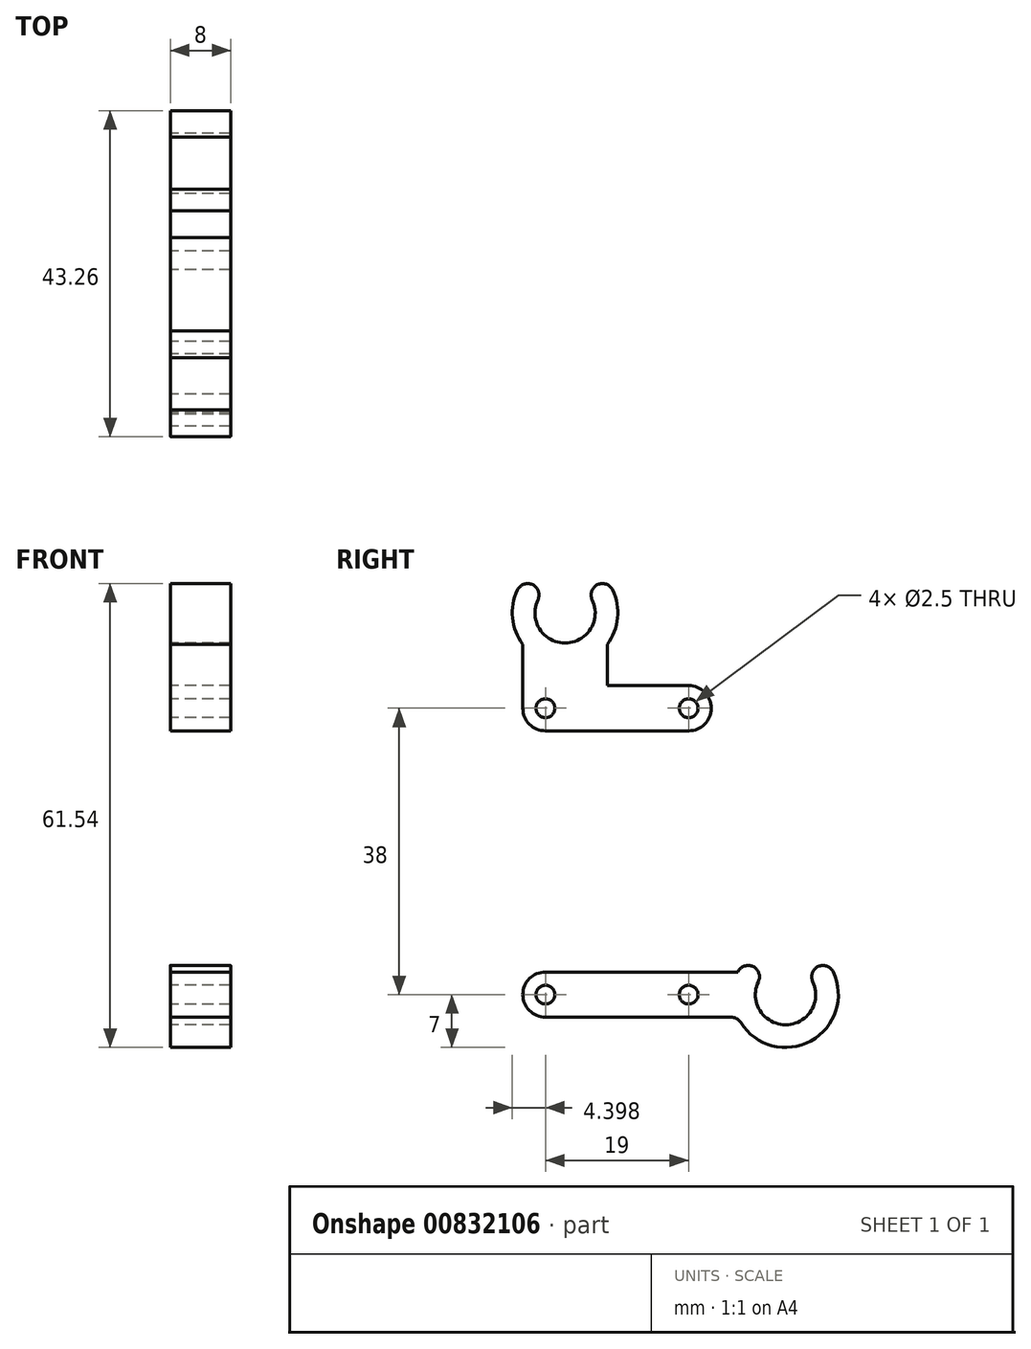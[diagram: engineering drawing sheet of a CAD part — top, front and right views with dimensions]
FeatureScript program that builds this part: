
annotation { "Feature Type Name" : "Feature", "Feature Type Description" : "" }
export const myFeature = defineFeature(function(context is Context, id is Id, definition is map)
    precondition{}
    {
        {
            var Q0;
            Q0=qCreatedBy(makeId("Right.planeOp"),FACE);
            var sketch = newSketch(context, id + "F0", { "sketchPlane" : qUnion([Q0])});
            skArc(sketch, "E0", {"start": v(-3, 53.3) * mm, "mid": v(0, 46.66) * mm, "end": v(3, 53.3) * mm});
            skArc(sketch, "E1", {"start": v(26.26, 2.65) * mm, "mid": v(29.26, -4) * mm, "end": v(32.26, 2.65) * mm});
            skCircle(sketch, "E2", {"center": v(-2.6, 0) * mm, "radius": 1.25 * mm});
            skCircle(sketch, "E3.0.1.0", {"center": v(-2.6, 38) * mm, "radius": 1.25 * mm});
            skCircle(sketch, "E3.1.0.0", {"center": v(16.4, 0) * mm, "radius": 1.25 * mm});
            skCircle(sketch, "E3.1.1.0", {"center": v(16.4, 38) * mm, "radius": 1.25 * mm});
            skLineSegment(sketch, "E3.direction1", {"start": v(-2.6, 0) * mm, "end": v(16.4, 0) * mm, "construction": true});
            skLineSegment(sketch, "E3.direction2", {"start": v(-2.6, 0) * mm, "end": v(-2.6, 38) * mm, "construction": true});
            skLineSegment(sketch, "E4.bottom", {"start": v(-7.8, 43) * mm, "end": v(21.6, 43) * mm, "construction": true});
            skLineSegment(sketch, "E4.top", {"start": v(-7.8, -5) * mm, "end": v(21.6, -5) * mm, "construction": true});
            skLineSegment(sketch, "E4.left", {"start": v(-7.8, 43) * mm, "end": v(-7.8, -5) * mm, "construction": true});
            skLineSegment(sketch, "E4.right", {"start": v(21.6, 43) * mm, "end": v(21.6, -5) * mm, "construction": true});
            skPoint(sketch, "E4.middle", {"position": v(6.9, 19) * mm});
            skPoint(sketch, "E4.middle.positionSnap0", {"position": v(-2.6, 19) * mm});
            skPoint(sketch, "E4.middle.positionSnap1", {"position": v(6.9, 0) * mm});
            skPoint(sketch, "E4.centerSnap0", {"position": v(-2.6, 19) * mm});
            skPoint(sketch, "E4.centerSnap1", {"position": v(6.9, 0) * mm});
            skLineSegment(sketch, "E5", {"start": v(0, 50.66) * mm, "end": v(0, 43) * mm, "construction": true});
            skLineSegment(sketch, "E6", {"start": v(29.26, 0) * mm, "end": v(21.6, 0) * mm, "construction": true});
            skArc(sketch, "E7", {"start": v(-2.6, 3) * mm, "mid": v(-5.6, 0) * mm, "end": v(-2.6, -3) * mm});
            skArc(sketch, "E8", {"start": v(22.94, -3) * mm, "mid": v(33.11, -5.84) * mm, "end": v(34.51, 4.63) * mm});
            skPoint(sketch, "E8.startSnap0", {"position": v(29.26, -4) * mm});
            skLineSegment(sketch, "E9", {"start": v(22.94, -3) * mm, "end": v(-2.6, -3) * mm});
            skLineSegment(sketch, "E10", {"start": v(-2.6, 3) * mm, "end": v(22.94, 3) * mm});
            skLineSegment(sketch, "E11", {"start": v(24.01, 4.63) * mm, "end": v(26.26, 2.65) * mm});
            skLineSegment(sketch, "E12", {"start": v(29.26, 0) * mm, "end": v(32.26, 2.65) * mm, "construction": true});
            skLineSegment(sketch, "E13", {"start": v(29.26, 0) * mm, "end": v(26.26, 2.65) * mm, "construction": true});
            skLineSegment(sketch, "E14", {"start": v(32.26, 2.65) * mm, "end": v(34.51, 4.63) * mm});
            skArc(sketch, "E15", {"start": v(-2.6, 35) * mm, "mid": v(-4.72, 35.88) * mm, "end": v(-5.6, 38) * mm});
            skArc(sketch, "E16", {"start": v(16.4, 41) * mm, "mid": v(19.4, 38) * mm, "end": v(16.4, 35) * mm});
            skLineSegment(sketch, "E17", {"start": v(16.4, 35) * mm, "end": v(-2.6, 35) * mm});
            skArc(sketch, "E18", {"start": v(-5.25, 55.3) * mm, "mid": v(-7, 50.94) * mm, "end": v(-5.6, 46.47) * mm});
            skArc(sketch, "E19", {"start": v(5.25, 55.3) * mm, "mid": v(7, 50.94) * mm, "end": v(5.6, 46.47) * mm});
            skLineSegment(sketch, "E20", {"start": v(-3, 53.3) * mm, "end": v(-5.25, 55.3) * mm});
            skLineSegment(sketch, "E21", {"start": v(3, 53.3) * mm, "end": v(5.25, 55.3) * mm});
            skLineSegment(sketch, "E22", {"start": v(0, 50.66) * mm, "end": v(3, 53.3) * mm, "construction": true});
            skLineSegment(sketch, "E23", {"start": v(0, 50.66) * mm, "end": v(-3, 53.3) * mm, "construction": true});
            skLineSegment(sketch, "E24", {"start": v(-5.6, 38) * mm, "end": v(-5.6, 46.47) * mm});
            skLineSegment(sketch, "E25", {"start": v(5.6, 46.47) * mm, "end": v(5.6, 41) * mm});
            skLineSegment(sketch, "E26", {"start": v(5.6, 41) * mm, "end": v(16.4, 41) * mm});
            skArc(sketch, "E27", {"start": v(24.01, 4.63) * mm, "mid": v(23.42, 3.85) * mm, "end": v(22.94, 3) * mm});
            skSolve(sketch);
        }
        {
            var Q0;
            Q0 = qSketchRegion(id + "F0", true);
            extrude(context, id + "F1", {"entities" : qUnion([Q0]), "depth" : 8 * mm, "offsetDistance" : 25 * mm});
        }
        {
            var Q0;
            Q0=makeQuery(id+"F1.opExtrude","SWEPT_EDGE",EDGE,{"disambiguationData":[OSD([sQuery(id+"F0.wireOp",EDGE,"E18"),sQuery(id+"F0.wireOp",EDGE,"E20")])]});
            var Q1;
            Q1=makeQuery(id+"F1.opExtrude","SWEPT_EDGE",EDGE,{"disambiguationData":[OSD([sQuery(id+"F0.wireOp",EDGE,"E19"),sQuery(id+"F0.wireOp",EDGE,"E21")])]});
            var Q2;
            Q2=makeQuery(id+"F1.opExtrude","SWEPT_EDGE",EDGE,{"disambiguationData":[OSD([sQuery(id+"F0.wireOp",EDGE,"E0"),sQuery(id+"F0.wireOp",EDGE,"E20")])]});
            var Q3;
            Q3=makeQuery(id+"F1.opExtrude","SWEPT_EDGE",EDGE,{"disambiguationData":[OSD([sQuery(id+"F0.wireOp",EDGE,"E0"),sQuery(id+"F0.wireOp",EDGE,"E21")])]});
            fillet(context, id + "F2", {"entities" : qUnion([Q0, Q1, Q2, Q3]), "radius" : 1.5 * mm, "tangentPropagation" : true, "allowEdgeOverflow" : false});
        }
        {
            var Q0;
            Q0=makeQuery(id+"F1.opExtrude","SWEPT_EDGE",EDGE,{"disambiguationData":[OSD([sQuery(id+"F0.wireOp",EDGE,"E1"),sQuery(id+"F0.wireOp",EDGE,"E14")])]});
            var Q1;
            Q1=makeQuery(id+"F1.opExtrude","SWEPT_EDGE",EDGE,{"disambiguationData":[OSD([sQuery(id+"F0.wireOp",EDGE,"E1"),sQuery(id+"F0.wireOp",EDGE,"E11")])]});
            var Q2;
            Q2=makeQuery(id+"F1.opExtrude","SWEPT_EDGE",EDGE,{"disambiguationData":[OSD([sQuery(id+"F0.wireOp",EDGE,"E8"),sQuery(id+"F0.wireOp",EDGE,"LXZMr7Pu-Qmbh-P0PK-dNyA-9Cm3fyl0Iijc")])]});
            var Q3;
            Q3=makeQuery(id+"F1.opExtrude","SWEPT_EDGE",EDGE,{"disambiguationData":[OSD([sQuery(id+"F0.wireOp",EDGE,"E11"),sQuery(id+"F0.wireOp",EDGE,"E27")])]});
            fillet(context, id + "F3", {"entities" : qUnion([Q0, Q1, Q2, Q3]), "radius" : 1.5 * mm, "tangentPropagation" : true, "allowEdgeOverflow" : false});
        }
    });
